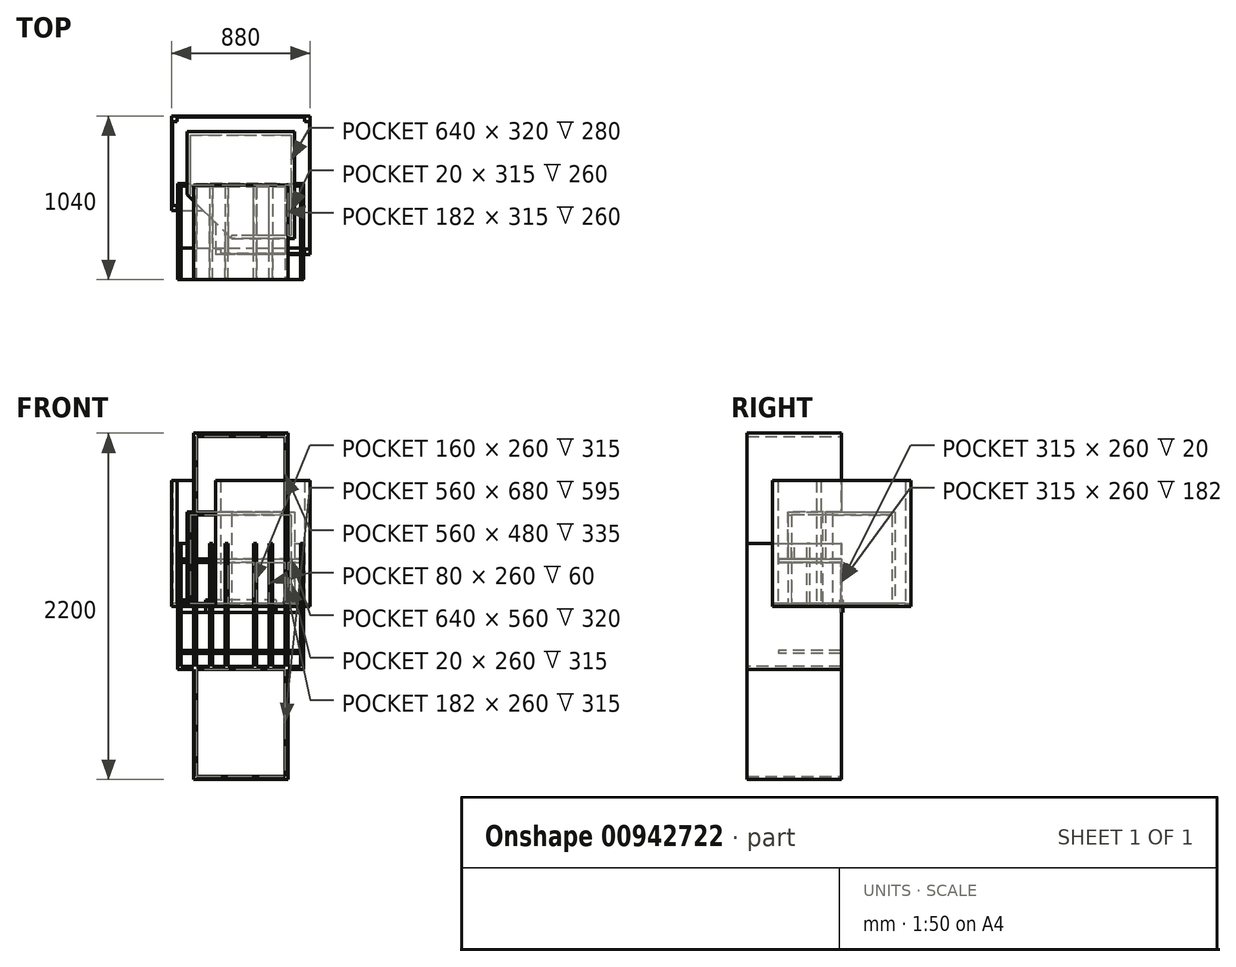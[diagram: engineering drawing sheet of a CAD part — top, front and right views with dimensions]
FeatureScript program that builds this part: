
annotation { "Feature Type Name" : "Feature", "Feature Type Description" : "" }
export const myFeature = defineFeature(function(context is Context, id is Id, definition is map)
    precondition{}
    {
        {
            var Q0;
            Q0=qCreatedBy(makeId("Right.planeOp"),FACE);
            var sketch = newSketch(context, id + "F0", { "sketchPlane" : qUnion([Q0])});
            skLineSegment(sketch, "E0.bottom", {"start": v(-10, 40) * mm, "end": v(10, 40) * mm});
            skLineSegment(sketch, "E0.top", {"start": v(-10, -40) * mm, "end": v(10, -40) * mm});
            skLineSegment(sketch, "E0.left", {"start": v(-10, 40) * mm, "end": v(-10, -40) * mm});
            skLineSegment(sketch, "E0.right", {"start": v(10, 40) * mm, "end": v(10, -40) * mm});
            skLineSegment(sketch, "E1", {"start": v(-10, 0) * mm, "end": v(0, 0) * mm, "construction": true});
            skLineSegment(sketch, "E2", {"start": v(0, 0) * mm, "end": v(10, 0) * mm, "construction": true});
            skLineSegment(sketch, "E3", {"start": v(0, -40) * mm, "end": v(0, 0) * mm, "construction": true});
            skLineSegment(sketch, "E4", {"start": v(0, 0) * mm, "end": v(0, 40) * mm, "construction": true});
            skSolve(sketch);
        }
        {
            var Q0;
            Q0=makeQuery(id+"F0.imprint","IMPRINT",FACE,{"disambiguationData":[TD([[makeQuery(id+"F0.imprint","IMPRINT",EDGE,{"derivedFrom":sQuery(id+"F0.wireOp",EDGE,"E0.bottom")}),-1.0]])]});
            extrude(context, id + "F1", {"entities" : qUnion([Q0]), "depth" : 200 * mm, "offsetDistance" : 25 * mm, "symmetric" : true});
        }
        {
            var Q0;
            Q0 = qSketchRegion(id + "F0", true);
            extrude(context, id + "F2", {"entities" : qUnion([Q0]), "depth" : 400 * mm, "offsetDistance" : 25 * mm, "symmetric" : true});
        }
        {
            var Q0;
            Q0=makeQuery(id+"F0.imprint","IMPRINT",FACE,{"disambiguationData":[TD([[makeQuery(id+"F0.imprint","IMPRINT",EDGE,{"derivedFrom":sQuery(id+"F0.wireOp",EDGE,"E0.bottom")}),-1.0]])]});
            extrude(context, id + "F3", {"entities" : qUnion([Q0]), "depth" : 600 * mm, "offsetDistance" : 25 * mm, "symmetric" : true});
        }
        {
            var Q0;
            Q0=makeQuery(id+"F0.imprint","IMPRINT",FACE,{"disambiguationData":[TD([[makeQuery(id+"F0.imprint","IMPRINT",EDGE,{"derivedFrom":sQuery(id+"F0.wireOp",EDGE,"E0.bottom")}),-1.0]])]});
            extrude(context, id + "F4", {"entities" : qUnion([Q0]), "depth" : 800 * mm, "offsetDistance" : 25 * mm, "symmetric" : true});
        }
        {
            var Q0;
            Q0=qCreatedBy(makeId("Front.planeOp"),FACE);
            var sketch = newSketch(context, id + "F5", { "sketchPlane" : qUnion([Q0])});
            skLineSegment(sketch, "E5.bottom", {"start": v(-300, 1100) * mm, "end": v(300, 1100) * mm});
            skLineSegment(sketch, "E5.top", {"start": v(-300, -1100) * mm, "end": v(300, -1100) * mm});
            skLineSegment(sketch, "E5.left", {"start": v(-300, 1100) * mm, "end": v(-300, -1100) * mm});
            skLineSegment(sketch, "E5.right", {"start": v(300, 1100) * mm, "end": v(300, -1100) * mm});
            skLineSegment(sketch, "E6", {"start": v(-300, 0) * mm, "end": v(0, 0) * mm, "construction": true});
            skLineSegment(sketch, "E7", {"start": v(0, 0) * mm, "end": v(300, 0) * mm, "construction": true});
            skLineSegment(sketch, "E8", {"start": v(0, 1100) * mm, "end": v(0, 0) * mm, "construction": true});
            skLineSegment(sketch, "E9", {"start": v(0, 0) * mm, "end": v(0, -1100) * mm, "construction": true});
            skLineSegment(sketch, "E10.bottom", {"start": v(-280, 1080) * mm, "end": v(280, 1080) * mm});
            skLineSegment(sketch, "E10.top", {"start": v(-280, -1080) * mm, "end": v(280, -1080) * mm});
            skLineSegment(sketch, "E10.left", {"start": v(-280, 1080) * mm, "end": v(-280, -1080) * mm});
            skLineSegment(sketch, "E10.right", {"start": v(280, 1080) * mm, "end": v(280, -1080) * mm});
            skSolve(sketch);
        }
        {
            var Q0;
            Q0 = qSketchRegion(id + "F5", true);
            extrude(context, id + "F6", {"entities" : qUnion([Q0]), "depth" : 600 * mm, "offsetDistance" : 25 * mm});
        }
        {
            var Q0;
            Q0=makeQuery(id+"F5.imprint","IMPRINT",FACE,{"disambiguationData":[TD([[makeQuery(id+"F5.imprint","IMPRINT",EDGE,{"derivedFrom":sQuery(id+"F5.wireOp",EDGE,"E10.bottom")}),-1.0]])]});
            var Q1;
            Q1=makeQuery(id+"F5.imprint","IMPRINT",FACE,{"disambiguationData":[TD([[makeQuery(id+"F5.imprint","IMPRINT",EDGE,{"derivedFrom":sQuery(id+"F5.wireOp",EDGE,"E10.top")}),1.0]])]});
            extrude(context, id + "F7", {"entities" : qUnion([Q0, Q1]), "operationType" : NewBodyOperationType.ADD, "depth" : 5 * mm, "offsetDistance" : 25 * mm});
        }
        {
            var Q0;
            Q0=qCreatedBy(makeId("Front.planeOp"),FACE);
            var sketch = newSketch(context, id + "F8", { "sketchPlane" : qUnion([Q0])});
            skLineSegment(sketch, "E11.bottom", {"start": v(-100, 400) * mm, "end": v(100, 400) * mm});
            skLineSegment(sketch, "E11.top", {"start": v(-100, -400) * mm, "end": v(100, -400) * mm});
            skLineSegment(sketch, "E11.left", {"start": v(-100, 400) * mm, "end": v(-100, -400) * mm});
            skLineSegment(sketch, "E11.right", {"start": v(100, 400) * mm, "end": v(100, -400) * mm});
            skLineSegment(sketch, "E12", {"start": v(-100, 0) * mm, "end": v(0, 0) * mm, "construction": true});
            skLineSegment(sketch, "E13", {"start": v(0, 0) * mm, "end": v(100, 0) * mm, "construction": true});
            skLineSegment(sketch, "E14", {"start": v(0, -400) * mm, "end": v(0, 0) * mm, "construction": true});
            skLineSegment(sketch, "E15", {"start": v(0, 0) * mm, "end": v(0, 400) * mm, "construction": true});
            skLineSegment(sketch, "E16", {"start": v(-80, 400) * mm, "end": v(-80, -380) * mm});
            skLineSegment(sketch, "E17", {"start": v(-80, -380) * mm, "end": v(80, -380) * mm});
            skLineSegment(sketch, "E18", {"start": v(80, -380) * mm, "end": v(80, 400) * mm});
            skSolve(sketch);
        }
        {
            var Q0;
            Q0=makeQuery(id+"F8.imprint","IMPRINT",FACE,{"disambiguationData":[TD([[makeQuery(id+"F8.imprint","IMPRINT",EDGE,{"derivedFrom":sQuery(id+"F8.wireOp",EDGE,"E11.top")}),1.0]])]});
            extrude(context, id + "F9", {"entities" : qUnion([Q0]), "depth" : 600 * mm, "offsetDistance" : 25 * mm});
        }
        {
            var Q0;
            {var subQ0=sQuery(id+"F8.wireOp",EDGE,"E16");Q0=makeQuery(id+"F8.imprint","IMPRINT",FACE,{"disambiguationData":[TD([[makeQuery(id+"F8.imprint","IMPRINT",EDGE,{"derivedFrom":subQ0}),1.0]])]});}
            extrude(context, id + "F10", {"entities" : qUnion([Q0]), "operationType" : NewBodyOperationType.ADD, "depth" : 5 * mm, "offsetDistance" : 25 * mm});
        }
        {
            var Q0;
            Q0=qCreatedBy(makeId("Front.planeOp"),FACE);
            var sketch = newSketch(context, id + "F11", { "sketchPlane" : qUnion([Q0])});
            skLineSegment(sketch, "E19.bottom", {"start": v(200, 400) * mm, "end": v(-200, 400) * mm});
            skLineSegment(sketch, "E19.top", {"start": v(200, -400) * mm, "end": v(-200, -400) * mm});
            skLineSegment(sketch, "E19.left", {"start": v(200, 400) * mm, "end": v(200, -400) * mm});
            skLineSegment(sketch, "E19.right", {"start": v(-200, 400) * mm, "end": v(-200, -400) * mm});
            skLineSegment(sketch, "E20", {"start": v(-200, 0) * mm, "end": v(0, 0) * mm, "construction": true});
            skLineSegment(sketch, "E21", {"start": v(0, 0) * mm, "end": v(200, 0) * mm, "construction": true});
            skLineSegment(sketch, "E22", {"start": v(0, 400) * mm, "end": v(0, 0) * mm, "construction": true});
            skLineSegment(sketch, "E23", {"start": v(0, 0) * mm, "end": v(0, -400) * mm, "construction": true});
            skLineSegment(sketch, "E24", {"start": v(-180, 400) * mm, "end": v(-180, -380) * mm});
            skLineSegment(sketch, "E25", {"start": v(-180, -380) * mm, "end": v(180, -380) * mm});
            skLineSegment(sketch, "E26", {"start": v(180, -380) * mm, "end": v(180, 400) * mm});
            skSolve(sketch);
        }
        {
            var Q0;
            Q0=makeQuery(id+"F11.imprint","IMPRINT",FACE,{"disambiguationData":[TD([[makeQuery(id+"F11.imprint","IMPRINT",EDGE,{"derivedFrom":sQuery(id+"F11.wireOp",EDGE,"E19.top")}),-1.0]])]});
            extrude(context, id + "F12", {"entities" : qUnion([Q0]), "depth" : 600 * mm, "offsetDistance" : 25 * mm});
        }
        {
            var Q0;
            {var subQ0=sQuery(id+"F11.wireOp",EDGE,"E24");Q0=makeQuery(id+"F11.imprint","IMPRINT",FACE,{"disambiguationData":[TD([[makeQuery(id+"F11.imprint","IMPRINT",EDGE,{"derivedFrom":subQ0}),1.0]])]});}
            extrude(context, id + "F13", {"entities" : qUnion([Q0]), "operationType" : NewBodyOperationType.ADD, "depth" : 5 * mm, "offsetDistance" : 25 * mm});
        }
        {
            var Q0;
            Q0=qCreatedBy(makeId("Front.planeOp"),FACE);
            var sketch = newSketch(context, id + "F14", { "sketchPlane" : qUnion([Q0])});
            skLineSegment(sketch, "E27.bottom", {"start": v(-400, 400) * mm, "end": v(400, 400) * mm});
            skLineSegment(sketch, "E27.top", {"start": v(-400, -400) * mm, "end": v(400, -400) * mm});
            skLineSegment(sketch, "E27.left", {"start": v(-400, 400) * mm, "end": v(-400, -400) * mm});
            skLineSegment(sketch, "E27.right", {"start": v(400, 400) * mm, "end": v(400, -400) * mm});
            skLineSegment(sketch, "E28", {"start": v(-400, 0) * mm, "end": v(0, 0) * mm, "construction": true});
            skLineSegment(sketch, "E29", {"start": v(0, 0) * mm, "end": v(400, 0) * mm, "construction": true});
            skLineSegment(sketch, "E30", {"start": v(0, -400) * mm, "end": v(0, 0) * mm, "construction": true});
            skLineSegment(sketch, "E31", {"start": v(0, 0) * mm, "end": v(0, 400) * mm, "construction": true});
            skLineSegment(sketch, "E32", {"start": v(-380, 400) * mm, "end": v(-380, -380) * mm});
            skLineSegment(sketch, "E33", {"start": v(-380, -380) * mm, "end": v(380, -380) * mm});
            skLineSegment(sketch, "E34", {"start": v(380, -380) * mm, "end": v(380, 400) * mm});
            skSolve(sketch);
        }
        {
            var Q0;
            Q0=makeQuery(id+"F14.imprint","IMPRINT",FACE,{"disambiguationData":[TD([[makeQuery(id+"F14.imprint","IMPRINT",EDGE,{"derivedFrom":sQuery(id+"F14.wireOp",EDGE,"E27.top")}),1.0]])]});
            extrude(context, id + "F15", {"entities" : qUnion([Q0]), "depth" : 600 * mm, "offsetDistance" : 25 * mm});
        }
        {
            var Q0;
            {var subQ0=sQuery(id+"F14.wireOp",EDGE,"E32");Q0=makeQuery(id+"F14.imprint","IMPRINT",FACE,{"disambiguationData":[TD([[makeQuery(id+"F14.imprint","IMPRINT",EDGE,{"derivedFrom":subQ0}),1.0]])]});}
            extrude(context, id + "F16", {"entities" : qUnion([Q0]), "operationType" : NewBodyOperationType.ADD, "depth" : 5 * mm, "offsetDistance" : 25 * mm});
        }
        {
            var Q0;
            Q0=qCreatedBy(makeId("Top.planeOp"),FACE);
            var sketch = newSketch(context, id + "F17", { "sketchPlane" : qUnion([Q0])});
            skLineSegment(sketch, "E35.bottom", {"start": v(440, 440) * mm, "end": v(-440, 440) * mm});
            skLineSegment(sketch, "E35.top", {"start": v(440, -440) * mm, "end": v(-160, -440) * mm});
            skLineSegment(sketch, "E35.left", {"start": v(440, 440) * mm, "end": v(440, -440) * mm});
            skLineSegment(sketch, "E35.right", {"start": v(-440, 440) * mm, "end": v(-440, -160) * mm});
            skLineSegment(sketch, "E36", {"start": v(-440, 0) * mm, "end": v(0, 0) * mm, "construction": true});
            skLineSegment(sketch, "E37", {"start": v(0, 0) * mm, "end": v(440, 0) * mm, "construction": true});
            skLineSegment(sketch, "E38", {"start": v(0, -440) * mm, "end": v(0, 0) * mm, "construction": true});
            skLineSegment(sketch, "E39", {"start": v(0, 0) * mm, "end": v(0, 440) * mm, "construction": true});
            skLineSegment(sketch, "E40", {"start": v(-440, -160) * mm, "end": v(-160, -160) * mm});
            skLineSegment(sketch, "E41", {"start": v(-160, -160) * mm, "end": v(-160, -440) * mm});
            skPoint(sketch, "E42.orphan", {"position": v(-440, -440) * mm});
            skLineSegment(sketch, "E43", {"start": v(-435, -130) * mm, "end": v(-435, 404) * mm});
            skLineSegment(sketch, "E44", {"start": v(-405, 434) * mm, "end": v(405, 434) * mm});
            skLineSegment(sketch, "E45", {"start": v(405, 434) * mm, "end": v(405, 404) * mm});
            skLineSegment(sketch, "E46", {"start": v(405, 404) * mm, "end": v(435, 404) * mm});
            skLineSegment(sketch, "E47", {"start": v(435, 404) * mm, "end": v(435, -405) * mm});
            skLineSegment(sketch, "E48", {"start": v(435, -405) * mm, "end": v(405, -405) * mm});
            skLineSegment(sketch, "E49", {"start": v(405, -405) * mm, "end": v(405, -435) * mm});
            skLineSegment(sketch, "E50", {"start": v(405, -435) * mm, "end": v(-130, -435) * mm});
            skLineSegment(sketch, "E51", {"start": v(-435, 404) * mm, "end": v(-405, 404) * mm});
            skLineSegment(sketch, "E52", {"start": v(-405, 404) * mm, "end": v(-405, 434) * mm});
            skLineSegment(sketch, "E53", {"start": v(-435, -130) * mm, "end": v(-405, -130) * mm});
            skLineSegment(sketch, "E54", {"start": v(-405, -130) * mm, "end": v(-405, -160) * mm});
            skLineSegment(sketch, "E55", {"start": v(-130, -435) * mm, "end": v(-130, -405) * mm});
            skLineSegment(sketch, "E56", {"start": v(-130, -405) * mm, "end": v(-160, -405) * mm});
            skSolve(sketch);
        }
        {
            var Q0;
            Q0=makeQuery(id+"F17.imprint","IMPRINT",FACE,{"disambiguationData":[TD([[makeQuery(id+"F17.imprint","IMPRINT",EDGE,{"derivedFrom":sQuery(id+"F17.wireOp",EDGE,"E43")}),-1.0]])]});
            var Q1;
            Q1=makeQuery(id+"F17.imprint","IMPRINT",FACE,{"disambiguationData":[TD([[makeQuery(id+"F17.imprint","IMPRINT",EDGE,{"derivedFrom":sQuery(id+"F17.wireOp",EDGE,"E35.bottom")}),1.0]])]});
            extrude(context, id + "F18", {"entities" : qUnion([Q0, Q1]), "depth" : 20 * mm, "offsetDistance" : 25 * mm});
        }
        {
            var Q0;
            Q0=makeQuery(id+"F17.imprint","IMPRINT",FACE,{"disambiguationData":[TD([[makeQuery(id+"F17.imprint","IMPRINT",EDGE,{"derivedFrom":sQuery(id+"F17.wireOp",EDGE,"E35.bottom")}),1.0]])]});
            extrude(context, id + "F19", {"entities" : qUnion([Q0]), "operationType" : NewBodyOperationType.ADD, "depth" : 800 * mm, "offsetDistance" : 25 * mm});
        }
        {
            var Q0;
            Q0=qCreatedBy(makeId("Top.planeOp"),FACE);
            var sketch = newSketch(context, id + "F20", { "sketchPlane" : qUnion([Q0])});
            skLineSegment(sketch, "E57.bottom", {"start": v(-60, -340) * mm, "end": v(340, -340) * mm});
            skLineSegment(sketch, "E57.top", {"start": v(-340, 340) * mm, "end": v(340, 340) * mm});
            skLineSegment(sketch, "E57.left", {"start": v(-340, -60) * mm, "end": v(-340, 340) * mm});
            skLineSegment(sketch, "E57.right", {"start": v(340, -340) * mm, "end": v(340, 340) * mm});
            skLineSegment(sketch, "E58", {"start": v(-340, -60) * mm, "end": v(-60, -340) * mm});
            skLineSegment(sketch, "E59", {"start": v(340, 0) * mm, "end": v(0, 0) * mm, "construction": true});
            skLineSegment(sketch, "E60", {"start": v(0, 0) * mm, "end": v(-340, 0) * mm, "construction": true});
            skLineSegment(sketch, "E61", {"start": v(0, 340) * mm, "end": v(0, 0) * mm, "construction": true});
            skLineSegment(sketch, "E62", {"start": v(0, 0) * mm, "end": v(0, -340) * mm, "construction": true});
            skLineSegment(sketch, "E63", {"start": v(-320, -60) * mm, "end": v(-320, 320) * mm});
            skLineSegment(sketch, "E64", {"start": v(-320, 320) * mm, "end": v(320, 320) * mm});
            skLineSegment(sketch, "E65", {"start": v(320, 320) * mm, "end": v(320, -320) * mm});
            skLineSegment(sketch, "E66", {"start": v(320, -320) * mm, "end": v(-60, -320) * mm});
            skLineSegment(sketch, "E67", {"start": v(-60, -340) * mm, "end": v(-60, -320) * mm});
            skLineSegment(sketch, "E68", {"start": v(-340, -60) * mm, "end": v(-320, -60) * mm});
            skSolve(sketch);
        }
        {
            var Q0;
            Q0=makeQuery(id+"F20.imprint","IMPRINT",FACE,{"disambiguationData":[TD([[makeQuery(id+"F20.imprint","IMPRINT",EDGE,{"derivedFrom":sQuery(id+"F20.wireOp",EDGE,"E58")}),1.0]])]});
            var Q1;
            Q1=makeQuery(id+"F20.imprint","IMPRINT",FACE,{"disambiguationData":[TD([[makeQuery(id+"F20.imprint","IMPRINT",EDGE,{"derivedFrom":sQuery(id+"F20.wireOp",EDGE,"E57.bottom")}),1.0]])]});
            extrude(context, id + "F21", {"entities" : qUnion([Q0, Q1]), "depth" : 600 * mm, "offsetDistance" : 25 * mm});
        }
        {
            var Q0;
            Q0=makeQuery(id+"F20.imprint","IMPRINT",FACE,{"disambiguationData":[TD([[makeQuery(id+"F20.imprint","IMPRINT",EDGE,{"derivedFrom":sQuery(id+"F20.wireOp",EDGE,"E58")}),1.0]])]});
            extrude(context, id + "F22", {"entities" : qUnion([Q0]), "operationType" : NewBodyOperationType.REMOVE, "depth" : 580 * mm, "offsetDistance" : 25 * mm, "hasSecondDirection" : true, "secondDirectionOppositeDirection" : false, "secondDirectionDepth" : 20 * mm});
        }
        {
            var Q0;
            Q0=qCreatedBy(makeId("Front.planeOp"),FACE);
            var sketch = newSketch(context, id + "F23", { "sketchPlane" : qUnion([Q0])});
            skLineSegment(sketch, "E69.bottom", {"start": v(-400, -300) * mm, "end": v(400, -300) * mm});
            skLineSegment(sketch, "E69.top", {"start": v(-400, 300) * mm, "end": v(400, 300) * mm});
            skLineSegment(sketch, "E69.left", {"start": v(-400, -300) * mm, "end": v(-400, 300) * mm});
            skLineSegment(sketch, "E69.right", {"start": v(400, -300) * mm, "end": v(400, 300) * mm});
            skLineSegment(sketch, "E70", {"start": v(-400, 0) * mm, "end": v(0, 0) * mm, "construction": true});
            skLineSegment(sketch, "E71", {"start": v(0, 0) * mm, "end": v(400, 0) * mm, "construction": true});
            skLineSegment(sketch, "E72", {"start": v(0, 300) * mm, "end": v(0, 0) * mm, "construction": true});
            skLineSegment(sketch, "E73", {"start": v(0, 0) * mm, "end": v(0, -300) * mm, "construction": true});
            skLineSegment(sketch, "E74.bottom", {"start": v(-380, -280) * mm, "end": v(380, -280) * mm});
            skLineSegment(sketch, "E74.top", {"start": v(-380, 280) * mm, "end": v(380, 280) * mm});
            skLineSegment(sketch, "E74.left", {"start": v(-380, -280) * mm, "end": v(-380, 280) * mm});
            skLineSegment(sketch, "E74.right", {"start": v(380, -280) * mm, "end": v(380, 280) * mm});
            skSolve(sketch);
        }
        {
            var Q0;
            Q0=makeQuery(id+"F23.imprint","IMPRINT",FACE,{"disambiguationData":[TD([[makeQuery(id+"F23.imprint","IMPRINT",EDGE,{"derivedFrom":sQuery(id+"F23.wireOp",EDGE,"E69.bottom")}),1.0]])]});
            extrude(context, id + "F24", {"entities" : qUnion([Q0]), "depth" : 400 * mm, "offsetDistance" : 25 * mm});
        }
        {
            var Q0;
            Q0=makeQuery(id+"F23.imprint","IMPRINT",FACE,{"disambiguationData":[TD([[makeQuery(id+"F23.imprint","IMPRINT",EDGE,{"derivedFrom":sQuery(id+"F23.wireOp",EDGE,"E74.bottom")}),1.0]])]});
            extrude(context, id + "F25", {"entities" : qUnion([Q0]), "operationType" : NewBodyOperationType.ADD, "depth" : 5 * mm, "offsetDistance" : 25 * mm});
        }
        {
            var Q0;
            Q0=qCreatedBy(makeId("Front.planeOp"),FACE);
            var sketch = newSketch(context, id + "F26", { "sketchPlane" : qUnion([Q0])});
            skLineSegment(sketch, "E75.bottom", {"start": v(100, 300) * mm, "end": v(-100, 300) * mm});
            skLineSegment(sketch, "E75.top", {"start": v(100, -300) * mm, "end": v(-100, -300) * mm});
            skLineSegment(sketch, "E75.left", {"start": v(100, 300) * mm, "end": v(100, -300) * mm});
            skLineSegment(sketch, "E75.right", {"start": v(-100, 300) * mm, "end": v(-100, -300) * mm});
            skLineSegment(sketch, "E76", {"start": v(-100, 0) * mm, "end": v(0, 0) * mm, "construction": true});
            skLineSegment(sketch, "E77", {"start": v(0, 0) * mm, "end": v(100, 0) * mm, "construction": true});
            skLineSegment(sketch, "E78", {"start": v(0, -300) * mm, "end": v(0, 0) * mm, "construction": true});
            skLineSegment(sketch, "E79", {"start": v(0, 0) * mm, "end": v(0, 300) * mm, "construction": true});
            skLineSegment(sketch, "E80.bottom", {"start": v(-80, -280) * mm, "end": v(80, -280) * mm});
            skLineSegment(sketch, "E80.top", {"start": v(-80, 280) * mm, "end": v(80, 280) * mm});
            skLineSegment(sketch, "E80.left", {"start": v(-80, -280) * mm, "end": v(-80, 280) * mm});
            skLineSegment(sketch, "E80.right", {"start": v(80, -280) * mm, "end": v(80, 280) * mm});
            skSolve(sketch);
        }
        {
            var Q0;
            Q0=makeQuery(id+"F26.imprint","IMPRINT",FACE,{"disambiguationData":[TD([[makeQuery(id+"F26.imprint","IMPRINT",EDGE,{"derivedFrom":sQuery(id+"F26.wireOp",EDGE,"E80.bottom")}),1.0]])]});
            extrude(context, id + "F27", {"entities" : qUnion([Q0]), "depth" : 5 * mm, "offsetDistance" : 25 * mm});
        }
        {
            var Q0;
            Q0=makeQuery(id+"F26.imprint","IMPRINT",FACE,{"disambiguationData":[TD([[makeQuery(id+"F26.imprint","IMPRINT",EDGE,{"derivedFrom":sQuery(id+"F26.wireOp",EDGE,"E75.bottom")}),1.0]])]});
            extrude(context, id + "F28", {"entities" : qUnion([Q0]), "operationType" : NewBodyOperationType.ADD, "depth" : 400 * mm, "offsetDistance" : 25 * mm});
        }
        {
            var Q0;
            Q0 = qSketchRegion(id + "F0", true);
            extrude(context, id + "F29", {"entities" : qUnion([Q0]), "depth" : 450 * mm, "offsetDistance" : 25 * mm, "symmetric" : true});
        }
        {
            var Q0;
            Q0=qCreatedBy(makeId("Front.planeOp"),FACE);
            var sketch = newSketch(context, id + "F30", { "sketchPlane" : qUnion([Q0])});
            skLineSegment(sketch, "E81.bottom", {"start": v(-300, -300) * mm, "end": v(300, -300) * mm});
            skLineSegment(sketch, "E81.top", {"start": v(-300, 300) * mm, "end": v(300, 300) * mm});
            skLineSegment(sketch, "E81.left", {"start": v(-300, -300) * mm, "end": v(-300, 300) * mm});
            skLineSegment(sketch, "E81.right", {"start": v(300, -300) * mm, "end": v(300, 300) * mm});
            skLineSegment(sketch, "E82", {"start": v(-300, 0) * mm, "end": v(0, 0) * mm, "construction": true});
            skLineSegment(sketch, "E83", {"start": v(0, 0) * mm, "end": v(300, 0) * mm, "construction": true});
            skLineSegment(sketch, "E84", {"start": v(0, -300) * mm, "end": v(0, 0) * mm, "construction": true});
            skLineSegment(sketch, "E85", {"start": v(0, 0) * mm, "end": v(0, 300) * mm, "construction": true});
            skLineSegment(sketch, "E86.bottom", {"start": v(-282, -282) * mm, "end": v(282, -282) * mm});
            skLineSegment(sketch, "E86.top", {"start": v(-282, 282) * mm, "end": v(282, 282) * mm});
            skLineSegment(sketch, "E86.left", {"start": v(-282, -282) * mm, "end": v(-282, 282) * mm});
            skLineSegment(sketch, "E86.right", {"start": v(282, -282) * mm, "end": v(282, 282) * mm});
            skSolve(sketch);
        }
        {
            var Q0;
            Q0=makeQuery(id+"F30.imprint","IMPRINT",FACE,{"disambiguationData":[TD([[makeQuery(id+"F30.imprint","IMPRINT",EDGE,{"derivedFrom":sQuery(id+"F30.wireOp",EDGE,"E86.bottom")}),1.0]])]});
            extrude(context, id + "F31", {"entities" : qUnion([Q0]), "depth" : 5 * mm, "offsetDistance" : 25 * mm});
        }
        {
            var Q0;
            Q0=makeQuery(id+"F30.imprint","IMPRINT",FACE,{"disambiguationData":[TD([[makeQuery(id+"F30.imprint","IMPRINT",EDGE,{"derivedFrom":sQuery(id+"F30.wireOp",EDGE,"E81.bottom")}),1.0]])]});
            extrude(context, id + "F32", {"entities" : qUnion([Q0]), "operationType" : NewBodyOperationType.ADD, "depth" : 400 * mm, "offsetDistance" : 25 * mm});
        }
    });
